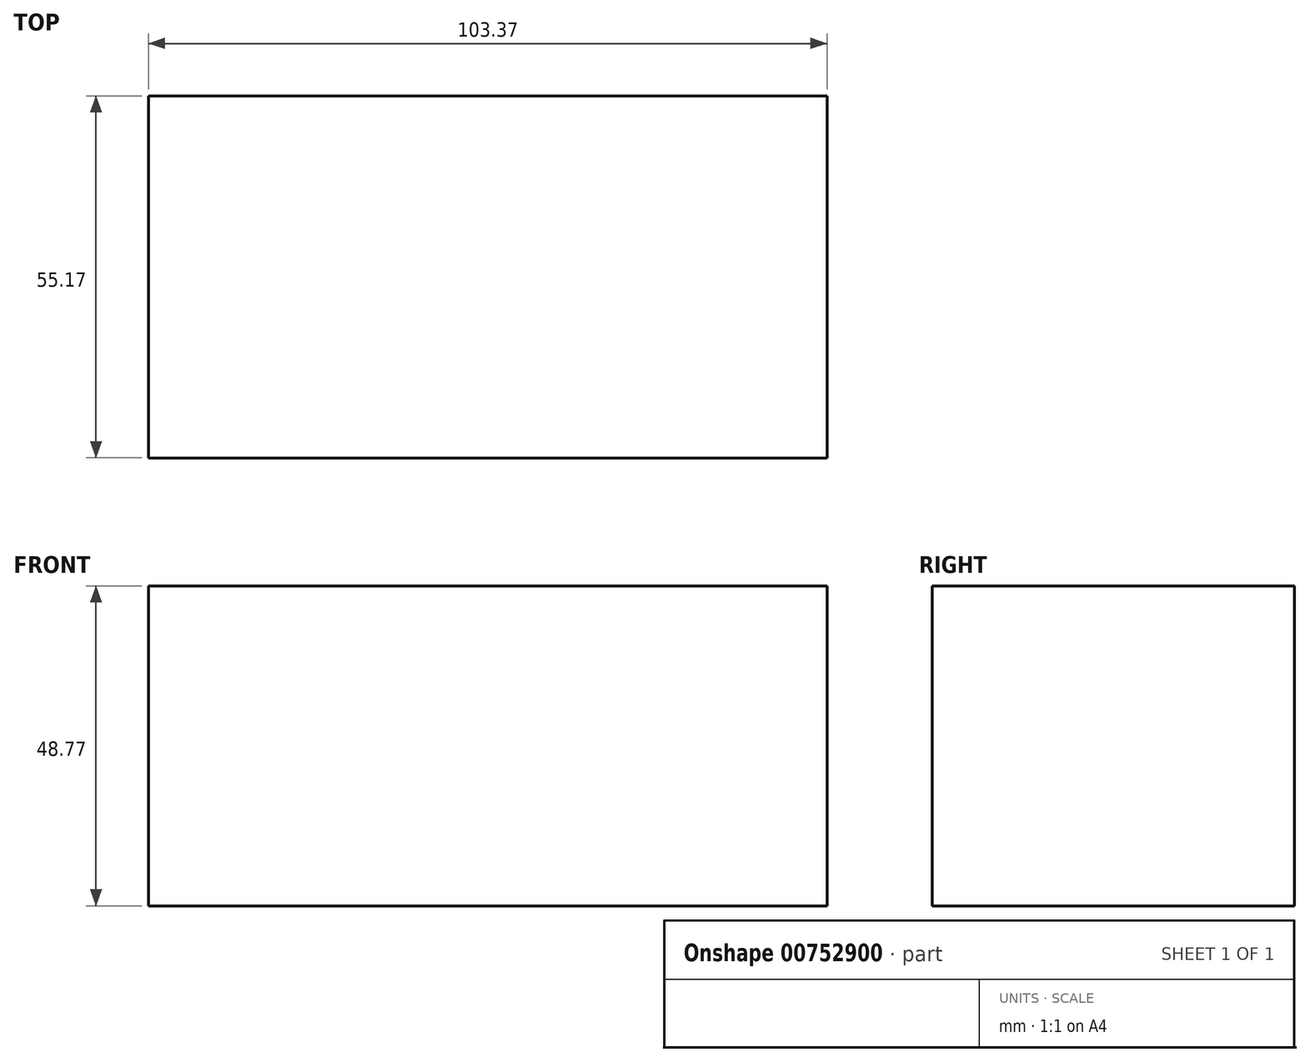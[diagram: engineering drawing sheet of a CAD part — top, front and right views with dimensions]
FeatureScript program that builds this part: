
annotation { "Feature Type Name" : "Feature", "Feature Type Description" : "" }
export const myFeature = defineFeature(function(context is Context, id is Id, definition is map)
    precondition{}
    {
        {
            var Q0;
            Q0=qCreatedBy(makeId("Top.planeOp"),FACE);
            var sketch = newSketch(context, id + "F0", { "sketchPlane" : qUnion([Q0])});
            skLineSegment(sketch, "E0.bottom", {"start": v(-51.17, -18.72) * mm, "end": v(52.2, -18.72) * mm});
            skLineSegment(sketch, "E0.top", {"start": v(-51.17, 36.45) * mm, "end": v(52.2, 36.45) * mm});
            skLineSegment(sketch, "E0.left", {"start": v(-51.17, -18.72) * mm, "end": v(-51.17, 36.45) * mm});
            skLineSegment(sketch, "E0.right", {"start": v(52.2, -18.72) * mm, "end": v(52.2, 36.45) * mm});
            skSolve(sketch);
        }
        {
            var Q0;
            Q0 = qSketchRegion(id + "F0", true);
            extrude(context, id + "F1", {"entities" : qUnion([Q0]), "depth" : 48.77 * mm, "offsetDistance" : 25.4 * mm});
        }
    });
